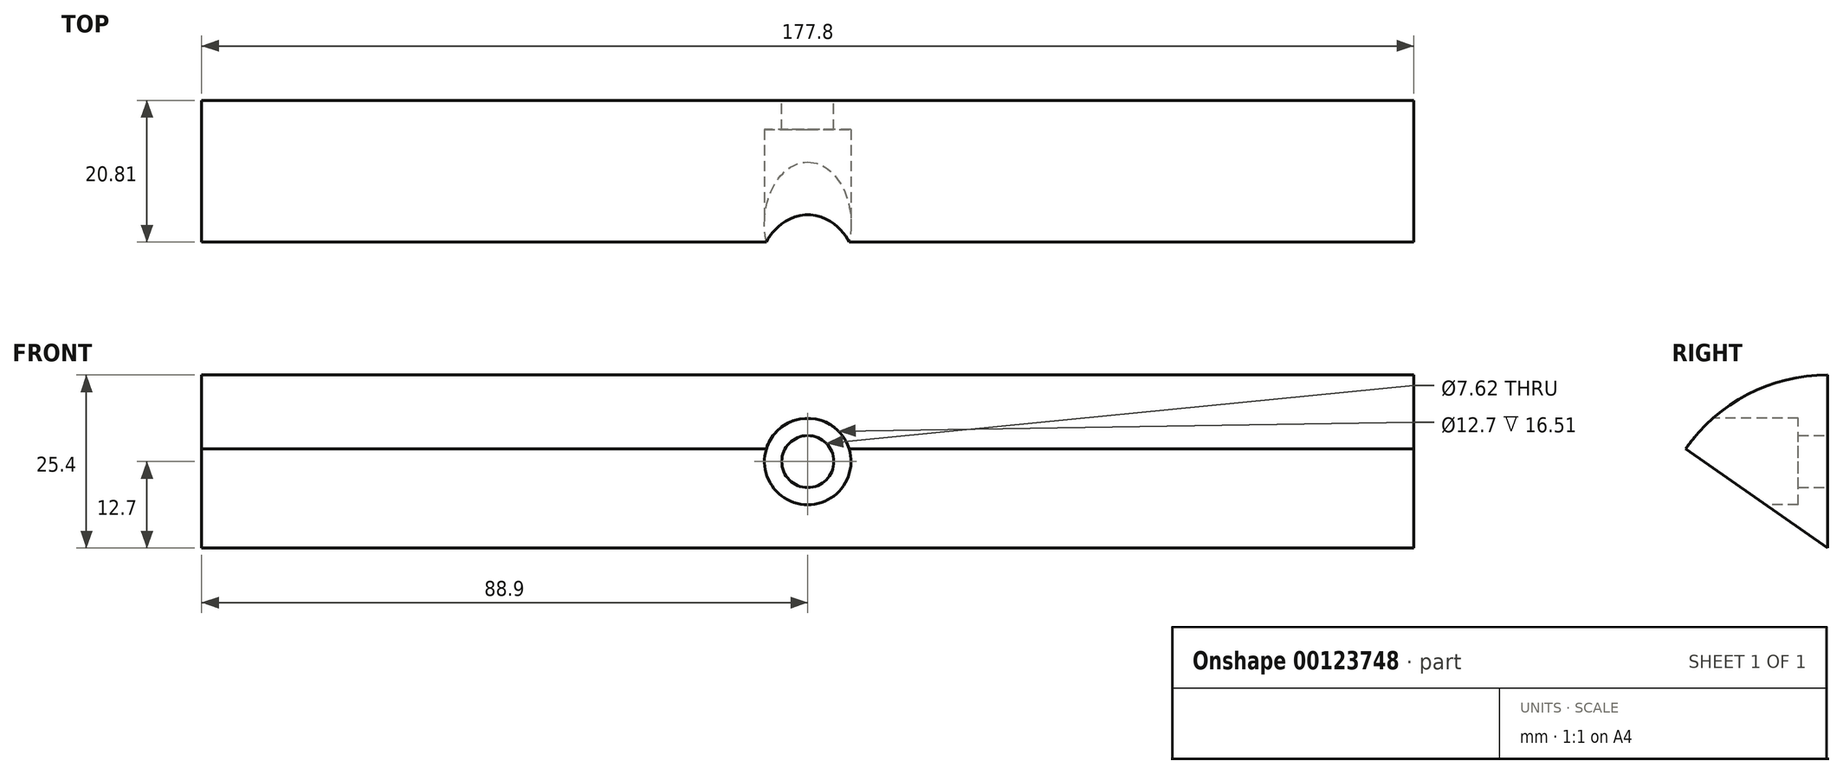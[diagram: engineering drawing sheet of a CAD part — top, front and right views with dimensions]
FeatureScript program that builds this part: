
annotation { "Feature Type Name" : "Feature", "Feature Type Description" : "" }
export const myFeature = defineFeature(function(context is Context, id is Id, definition is map)
    precondition{}
    {
        {
            var Q0;
            Q0=qCreatedBy(makeId("Front.planeOp"),FACE);
            var sketch = newSketch(context, id + "F0", { "sketchPlane" : qUnion([Q0])});
            skLineSegment(sketch, "E0.bottom", {"start": v(0, 0) * mm, "end": v(177.8, 0) * mm});
            skLineSegment(sketch, "E0.top", {"start": v(0, 25.4) * mm, "end": v(177.8, 25.4) * mm});
            skLineSegment(sketch, "E0.left", {"start": v(0, 0) * mm, "end": v(0, 25.4) * mm});
            skLineSegment(sketch, "E0.right", {"start": v(177.8, 0) * mm, "end": v(177.8, 25.4) * mm});
            skSolve(sketch);
        }
        {
            var Q0;
            Q0=makeQuery(id+"F0.imprint","IMPRINT",FACE,{"disambiguationData":[TD([[makeQuery(id+"F0.imprint","IMPRINT",EDGE,{"derivedFrom":sQuery(id+"F0.wireOp",EDGE,"E0.bottom")}),1.0]])]});
            var Q1;
            Q1=sQuery(id+"F0.wireOp",EDGE,"E0.bottom");
            revolve(context, id + "F1", {"entities" : qUnion([Q0]), "axis" : qUnion([Q1]), "revolveType" : RevolveType.ONE_DIRECTION, "angle" : 55 * degree});
        }
        {
            var Q0;
            Q0=qCreatedBy(makeId("Front.planeOp"),FACE);
            var sketch = newSketch(context, id + "F2", { "sketchPlane" : qUnion([Q0])});
            skLineSegment(sketch, "E1", {"start": v(0, 0) * mm, "end": v(88.9, 0) * mm});
            skLineSegment(sketch, "E2", {"start": v(88.9, 0) * mm, "end": v(88.9, 12.7) * mm});
            skCircle(sketch, "E3", {"center": v(88.9, 12.7) * mm, "radius": 3.81 * mm});
            skSolve(sketch);
        }
        {
            var Q0;
            Q0 = qSketchRegion(id + "F2", true);
            extrude(context, id + "F3", {"entities" : qUnion([Q0]), "operationType" : NewBodyOperationType.REMOVE, "endBound" : BoundingType.THROUGH_ALL, "depth" : 25.4 * mm});
        }
        {
            var Q0;
            Q0=makeQuery(id+"F1.opRevolve","CAP_VERTEX",VERTEX,{"disambiguationData":[OSD([sQuery(id+"F0.wireOp",EDGE,"E0.top"),sQuery(id+"F0.wireOp",EDGE,"E0.left")])],"isStart":false});
            var Q1;
            Q1=qCreatedBy(makeId("Front.planeOp"),FACE);
            cPlane(context, id + "F4", {"entities" : qUnion([Q0, Q1]), "cplaneType" : CPlaneType.PLANE_POINT, "offset" : 25.4 * mm, "width" : 152.4 * mm, "height" : 152.4 * mm});
        }
        {
            var Q0;
            Q0=qCreatedBy(id+"F4.planeOp",FACE);
            var sketch = newSketch(context, id + "F5", { "sketchPlane" : qUnion([Q0])});
            skCircle(sketch, "E4", {"center": v(88.9, 12.7) * mm, "radius": 6.35 * mm});
            skSolve(sketch);
        }
        {
            var Q0;
            Q0=makeQuery(id+"F5.imprint","IMPRINT",FACE,{"disambiguationData":[TD([[makeQuery(id+"F5.imprint","IMPRINT",EDGE,{"derivedFrom":sQuery(id+"F5.wireOp",EDGE,"E4")}),1.0]])]});
            extrude(context, id + "F6", {"entities" : qUnion([Q0]), "operationType" : NewBodyOperationType.REMOVE, "oppositeDirection" : true, "depth" : 16.5 * mm});
        }
    });
